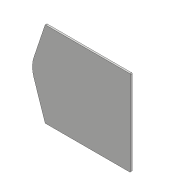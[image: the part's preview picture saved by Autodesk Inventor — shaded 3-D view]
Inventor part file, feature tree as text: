
AUTODESK INVENTOR PART (.ipt)
format: ipt  version: 2018 (Build 220112000, 112)  size: 199,168 bytes
history: native  units: mm
features: projected_geometry x8, sketch x6, extrude x4, fillet x3, hole x2
ambient origin geometry x8: Origin, YZ Plane, XZ Plane, XY Plane, X Axis, Y Axis, Z Axis, Center Point
bodies: Solid1 (feature_tree)
feature tree (23):
  extrude  "Extrusion1"  Depth=30.0mm
  extrude  "Extrusion2"  Depth=150.0mm
  extrude  "Extrusion3"  Depth=3.0mm TaperAngle=0.0deg
  extrude  "Extrusion4"  Depth=15.0mm TaperAngle=0.0deg
  fillet  "Fillet1"  Radius=12.5mm
  hole  "Hole1"  [1 undecoded]
  fillet  "Fillet2"  Radius=5.0mm
  hole  "Hole2"  [1 undecoded]
  fillet  "Fillet3"  Radius=5.0mm
  sketch  "Sketch1"  dims[d0=100.0mm d1=30.0mm]
  sketch  "Sketch2"  dims[d2=30.0mm d3=0.0mm d4=150.0mm]
  projected_geometry  "Projected Loop1"
  sketch  "Sketch3"  dims[d5=150.0mm d6=3.0mm d7=0.0mm]
  projected_geometry  "Projected Loop2"
  sketch  "Sketch4"  dims[d8=40.0mm d9=15.0mm d10=0.0mm d11=12.5mm]
  projected_geometry  "Projected Loop3"
  sketch  "Sketch5"  dims[d12=21.0mm d13=8.0mm d14=5.0mm]
  projected_geometry  "Projected Loop4"
  sketch  "Sketch6"  dims[d15=5.0mm d16=5.0mm d17=5.0mm d18=5.0mm d19=7.0mm d20=0.0mm d21=2.0mm d22=20.0mm d23=4.5mm d24=6.0mm d25=8.0mm d26=55.0mm d27=90.0deg d28=8.0mm d29=20.594885mm d30=1.0mm d31=1.567mm d32=10.0mm d33=8.0mm d34=55.0mm d35=90.0deg d36=10.0mm d37=20.594885mm d38=1.0mm]
  projected_geometry  "Projected Loop5"
  projected_geometry  "Projected Loop6"
  projected_geometry  "Projected Loop7"
  projected_geometry  "Projected Loop8"
note: 2 required parameter values undecoded (feature->parameter linkage not recoverable at this tier; creation-order binding heuristic only, values carry confidence <= 0.55)
